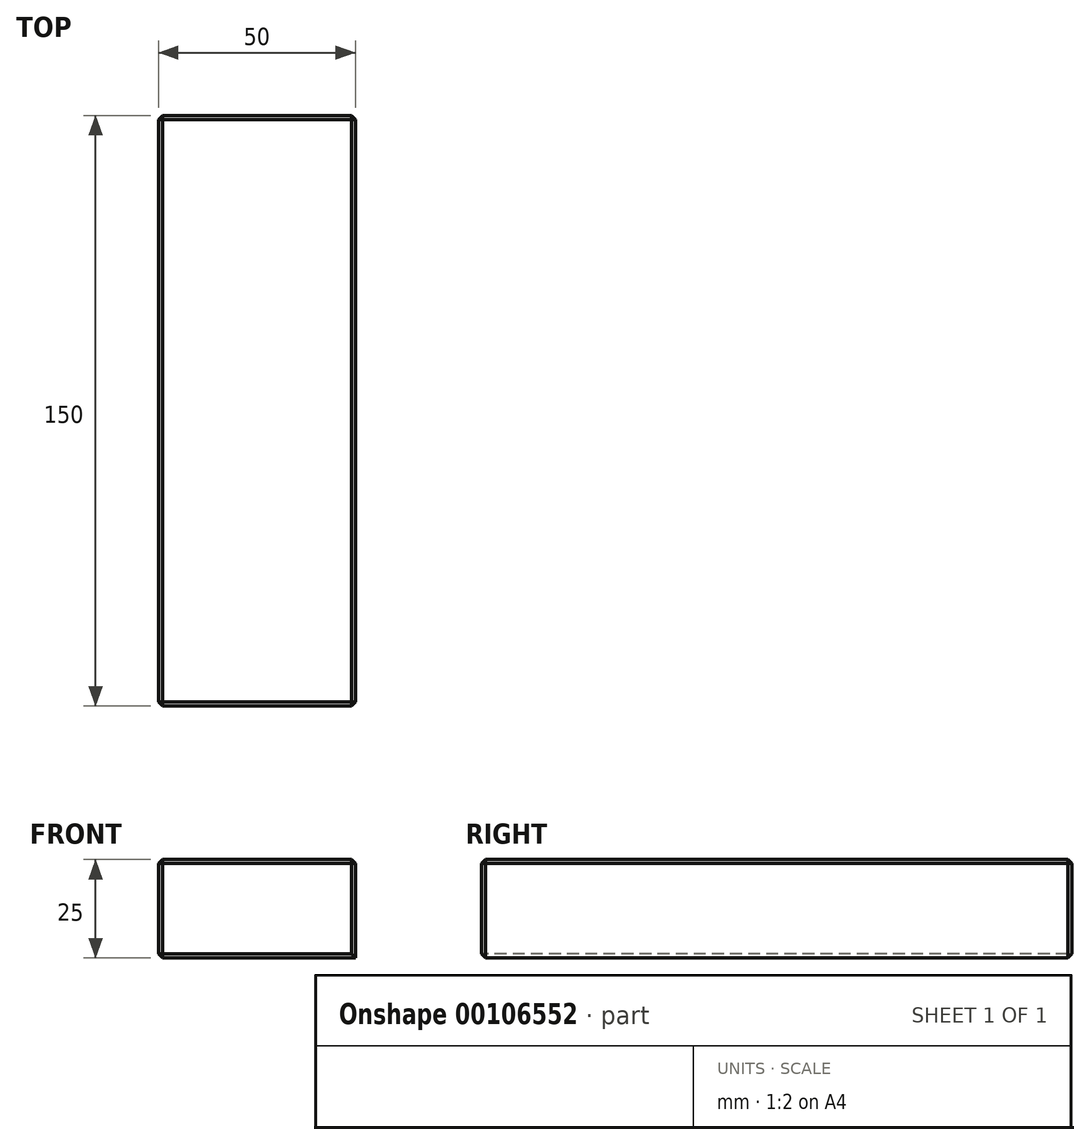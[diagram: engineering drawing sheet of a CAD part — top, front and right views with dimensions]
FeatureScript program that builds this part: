
annotation { "Feature Type Name" : "Feature", "Feature Type Description" : "" }
export const myFeature = defineFeature(function(context is Context, id is Id, definition is map)
    precondition{}
    {
        {
            var Q0;
            Q0=qCreatedBy(makeId("Front.planeOp"),FACE);
            var sketch = newSketch(context, id + "F0", { "sketchPlane" : qUnion([Q0])});
            skLineSegment(sketch, "E0.bottom", {"start": v(25, -12.5) * mm, "end": v(-25, -12.5) * mm});
            skLineSegment(sketch, "E0.top", {"start": v(25, 12.5) * mm, "end": v(-25, 12.5) * mm});
            skLineSegment(sketch, "E0.left", {"start": v(25, -12.5) * mm, "end": v(25, 12.5) * mm});
            skLineSegment(sketch, "E0.right", {"start": v(-25, -12.5) * mm, "end": v(-25, 12.5) * mm});
            skPoint(sketch, "E0.middle", {"position": v(0, 0) * mm});
            skSolve(sketch);
        }
        {
            var Q0;
            Q0=makeQuery(id+"F0.imprint","IMPRINT",FACE,{"disambiguationData":[TD([[makeQuery(id+"F0.imprint","IMPRINT",EDGE,{"derivedFrom":sQuery(id+"F0.wireOp",EDGE,"E0.bottom")}),-1.0]])]});
            extrude(context, id + "F1", {"entities" : qUnion([Q0]), "endBound" : BoundingType.SYMMETRIC, "depth" : 150 * mm});
        }
        {
            var Q0;
            Q0=makeQuery(id+"F1.opExtrude","SWEPT_EDGE",EDGE,{"disambiguationData":[OSD([sQuery(id+"F0.wireOp",EDGE,"E0.top"),sQuery(id+"F0.wireOp",EDGE,"E0.right")])]});
            var Q1;
            Q1=makeQuery(id+"F1.opExtrude","CAP_EDGE",EDGE,{"disambiguationData":[OSD([sQuery(id+"F0.wireOp",EDGE,"E0.top")])],"isStart":true});
            var Q2;
            Q2=makeQuery(id+"F1.opExtrude","CAP_EDGE",EDGE,{"disambiguationData":[OSD([sQuery(id+"F0.wireOp",EDGE,"E0.left")])],"isStart":true});
            var Q3;
            Q3=makeQuery(id+"F1.opExtrude","CAP_EDGE",EDGE,{"disambiguationData":[OSD([sQuery(id+"F0.wireOp",EDGE,"E0.bottom")])],"isStart":true});
            var Q4;
            Q4=makeQuery(id+"F1.opExtrude","CAP_EDGE",EDGE,{"disambiguationData":[OSD([sQuery(id+"F0.wireOp",EDGE,"E0.right")])],"isStart":true});
            var Q5;
            Q5=makeQuery(id+"F1.opExtrude","SWEPT_EDGE",EDGE,{"disambiguationData":[OSD([sQuery(id+"F0.wireOp",EDGE,"E0.bottom"),sQuery(id+"F0.wireOp",EDGE,"E0.right")])]});
            var Q6;
            Q6=makeQuery(id+"F1.opExtrude","SWEPT_EDGE",EDGE,{"disambiguationData":[OSD([sQuery(id+"F0.wireOp",EDGE,"E0.top"),sQuery(id+"F0.wireOp",EDGE,"E0.left")])]});
            var Q7;
            Q7=makeQuery(id+"F1.opExtrude","CAP_EDGE",EDGE,{"disambiguationData":[OSD([sQuery(id+"F0.wireOp",EDGE,"E0.right")])],"isStart":false});
            var Q8;
            Q8=makeQuery(id+"F1.opExtrude","CAP_EDGE",EDGE,{"disambiguationData":[OSD([sQuery(id+"F0.wireOp",EDGE,"E0.left")])],"isStart":false});
            var Q9;
            Q9=makeQuery(id+"F1.opExtrude","CAP_EDGE",EDGE,{"disambiguationData":[OSD([sQuery(id+"F0.wireOp",EDGE,"E0.bottom")])],"isStart":false});
            var Q10;
            Q10=makeQuery(id+"F1.opExtrude","CAP_EDGE",EDGE,{"disambiguationData":[OSD([sQuery(id+"F0.wireOp",EDGE,"E0.top")])],"isStart":false});
            chamfer(context, id + "F2", {"entities" : qUnion([Q0, Q1, Q2, Q3, Q4, Q5, Q6, Q7, Q8, Q9, Q10]), "width" : 1 * mm, "tangentPropagation" : true});
        }
    });
